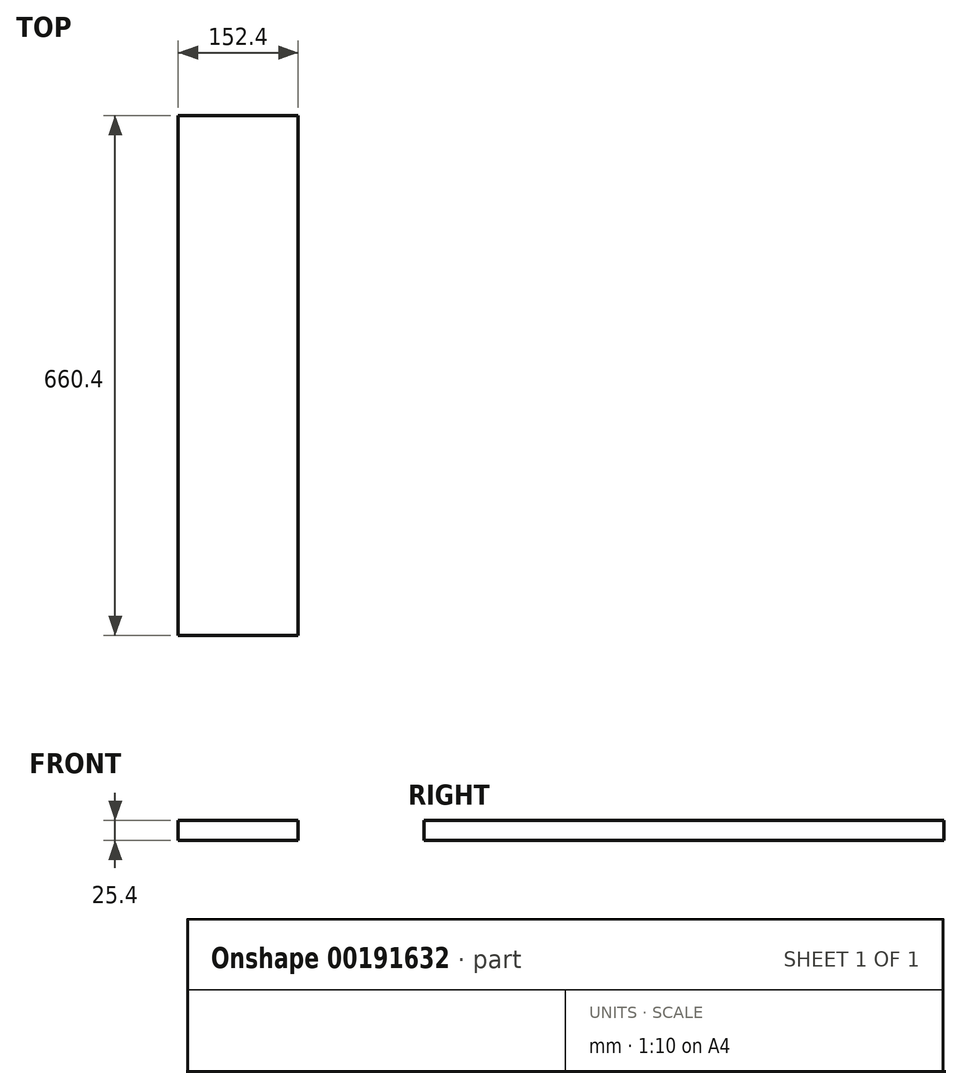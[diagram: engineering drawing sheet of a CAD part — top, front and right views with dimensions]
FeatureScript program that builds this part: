
annotation { "Feature Type Name" : "Feature", "Feature Type Description" : "" }
export const myFeature = defineFeature(function(context is Context, id is Id, definition is map)
    precondition{}
    {
        {
            var Q0;
            Q0=qCreatedBy(makeId("Top.planeOp"),FACE);
            var sketch = newSketch(context, id + "F0", { "sketchPlane" : qUnion([Q0])});
            skLineSegment(sketch, "E0.bottom", {"start": v(0, 0) * mm, "end": v(152.4, 0) * mm});
            skLineSegment(sketch, "E0.top", {"start": v(0, -660.4) * mm, "end": v(152.4, -660.4) * mm});
            skLineSegment(sketch, "E0.left", {"start": v(0, 0) * mm, "end": v(0, -660.4) * mm});
            skLineSegment(sketch, "E0.right", {"start": v(152.4, 0) * mm, "end": v(152.4, -660.4) * mm});
            skSolve(sketch);
        }
        {
            var Q0;
            Q0=makeQuery(id+"F0.imprint","IMPRINT",FACE,{"disambiguationData":[TD([[makeQuery(id+"F0.imprint","IMPRINT",EDGE,{"derivedFrom":sQuery(id+"F0.wireOp",EDGE,"E0.bottom")}),-1.0]])]});
            extrude(context, id + "F1", {"entities" : qUnion([Q0]), "depth" : 25.4 * mm});
        }
    });
